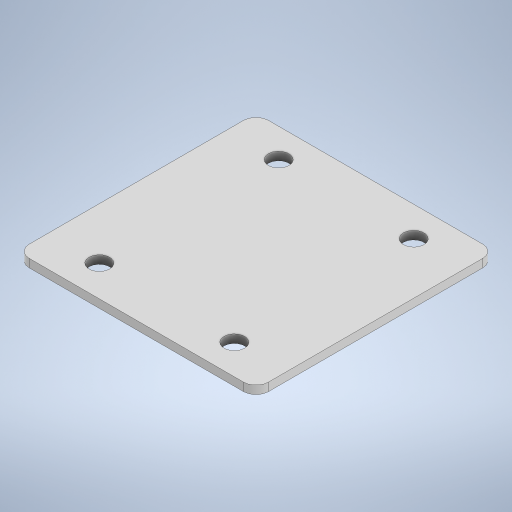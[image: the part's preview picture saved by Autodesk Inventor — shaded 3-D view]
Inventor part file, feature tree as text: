
AUTODESK INVENTOR PART (.ipt)
format: ipt  version: 2024.2 (Build 282272000, 272)  size: 236,544 bytes
history: native  units: mm
features: extrude x1, fillet x1, sketch x1
ambient origin geometry x8: Origin, YZ Plane, XZ Plane, XY Plane, X Axis, Y Axis, Z Axis, Center Point
bodies: Solid1 (feature_tree)
feature tree (3):
  extrude  "Extrusion1"  Depth=58.0mm
  fillet  "Fillet1"  Radius=5.0mm
  sketch  "Sketch1"  dims[d0=58.0mm d1=58.0mm d2=5.0mm d3=5.0mm d4=5.0mm d5=5.0mm d7=12.5mm d8=33.0mm d9=33.0mm d10=7.25mm d11=7.0mm d14=43.5mm d15=43.5mm d16=2.0mm d17=0.0mm d18=3.0mm d19=0.0mm d20=0.0mm d21=0.0mm]
